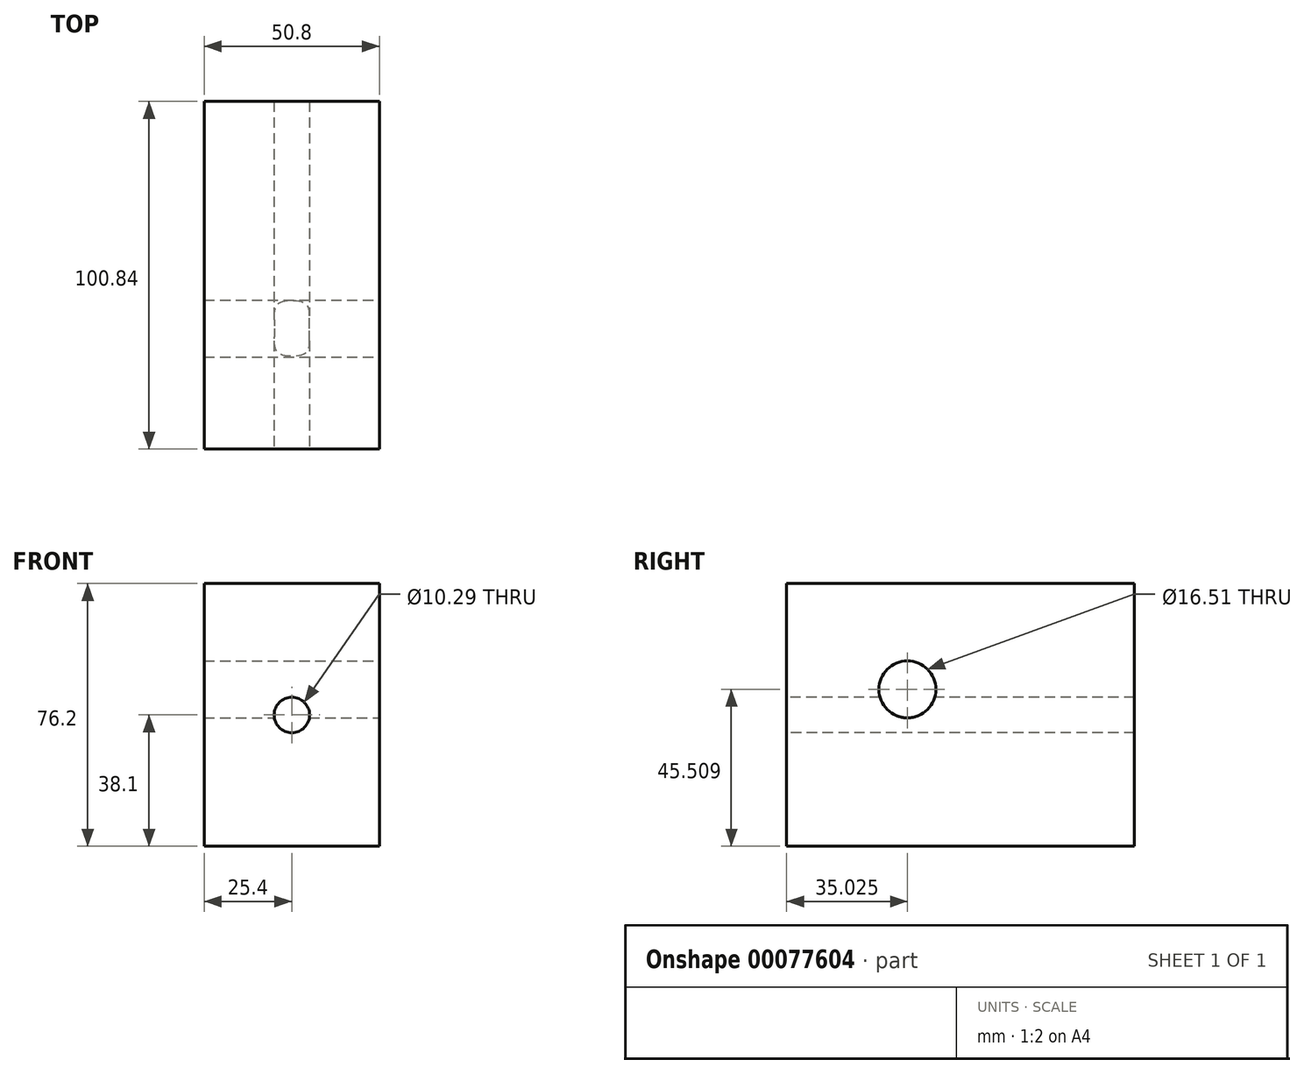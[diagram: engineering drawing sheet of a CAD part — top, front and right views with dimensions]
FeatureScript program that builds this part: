
annotation { "Feature Type Name" : "Feature", "Feature Type Description" : "" }
export const myFeature = defineFeature(function(context is Context, id is Id, definition is map)
    precondition{}
    {
        {
            var Q0;
            Q0=qCreatedBy(makeId("Front.planeOp"),FACE);
            var sketch = newSketch(context, id + "F0", { "sketchPlane" : qUnion([Q0])});
            skLineSegment(sketch, "E0.bottom", {"start": v(0, 0) * mm, "end": v(50.8, 0) * mm});
            skLineSegment(sketch, "E0.top", {"start": v(0, 76.2) * mm, "end": v(50.8, 76.2) * mm});
            skLineSegment(sketch, "E0.left", {"start": v(0, 0) * mm, "end": v(0, 76.2) * mm});
            skLineSegment(sketch, "E0.right", {"start": v(50.8, 0) * mm, "end": v(50.8, 76.2) * mm});
            skCircle(sketch, "E1", {"center": v(25.4, 38.1) * mm, "radius": 5.14 * mm});
            skSolve(sketch);
        }
        {
            var Q0;
            Q0 = qSketchRegion(id + "F0", true);
            extrude(context, id + "F1", {"entities" : qUnion([Q0]), "oppositeDirection" : true, "depth" : 100.84 * mm, "offsetDistance" : 25.4 * mm});
        }
        {
            var Q0;
            Q0=makeQuery(id+"F1.opExtrude","SWEPT_FACE",FACE,{"disambiguationData":[OSD([sQuery(id+"F0.wireOp",EDGE,"E0.right")])]});
            var sketch = newSketch(context, id + "F2", { "sketchPlane" : qUnion([Q0])});
            skCircle(sketch, "E2", {"center": v(35.02, 45.5) * mm, "radius": 8.26 * mm});
            skSolve(sketch);
        }
        {
            var Q0;
            Q0 = qSketchRegion(id + "F2", true);
            extrude(context, id + "F3", {"entities" : qUnion([Q0]), "operationType" : NewBodyOperationType.REMOVE, "oppositeDirection" : true, "depth" : 98.04 * mm, "offsetDistance" : 25.4 * mm});
        }
    });
